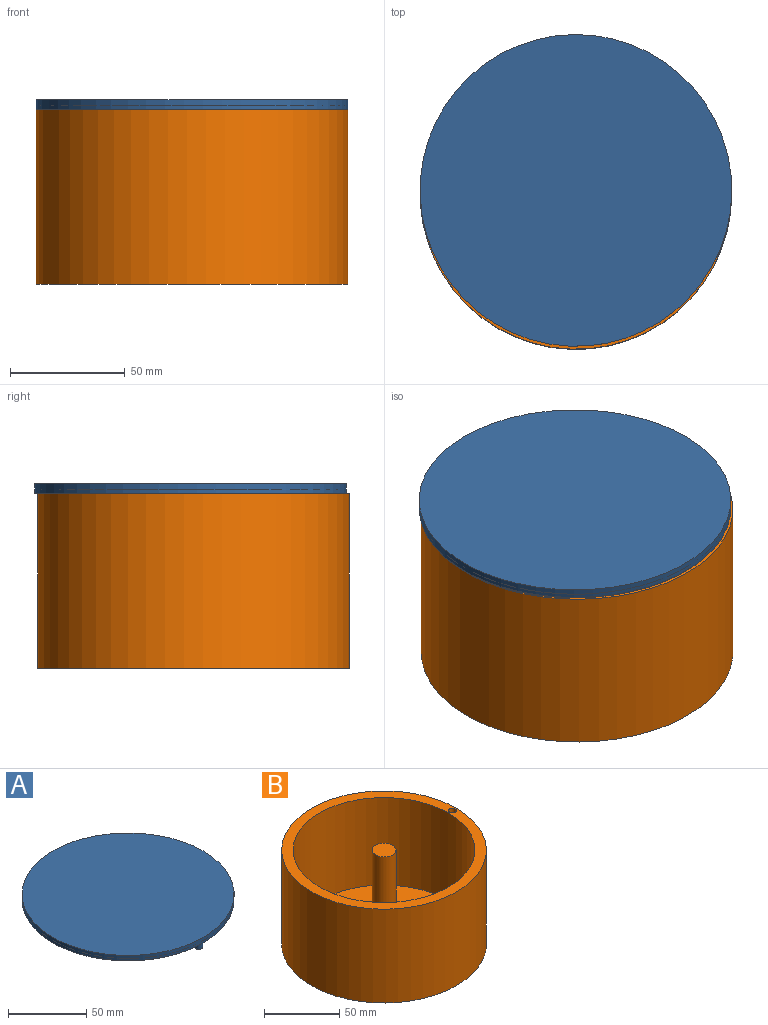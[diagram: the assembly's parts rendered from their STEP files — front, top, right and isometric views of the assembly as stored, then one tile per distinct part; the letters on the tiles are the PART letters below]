
ASSEMBLY  parts=2 mates=1
PART A: 9 faces, bbox 137.6x135.9x73.7 mm
  f0: torus R=4.95mm, axis (0,0,1), area 64.3mm2, adj f1,f5,f6,f7
  f1: cylinder r=2.41mm len=68.58mm, axis (0,0,-1), area 1039.8mm2, adj f0,f2,f6
  f2: plane 4.83x4.83mm, normal (0,0,-1), area 18.3mm2, adj f1
  f3: cylinder r=67.95mm len=135.89mm, axis (0,0,-1), area 1843.4mm2, adj f4,f8
  f4: plane 135.89x135.89mm, normal (0,0,1), area 14503.2mm2, adj f3
  f5: plane 135.26x135.16mm, normal (0,0,-1), area 14298.2mm2, adj f0,f7
  f6: bspline ~7.15x2.82mm, area 11.8mm2, adj f0,f1,f7
  f7: cylinder r=67.63mm len=135.26mm, axis (0,0,1), area 754.8mm2, adj f0,f5,f6,f8
  f8: plane 135.89x135.89mm, normal (0,0,-1), area 135.2mm2, adj f3,f7
PART B: 9 faces, bbox 135.9x135.9x76.2 mm
  f0: cylinder r=2.54mm len=71.12mm, axis (0,0,-1), area 1135mm2, adj f3,f8
  f1: cylinder r=60.32mm len=120.65mm, axis (0,0,-1), area 26956.8mm2, adj f3,f5
  f2: cylinder r=67.95mm len=135.89mm, axis (0,0,-1), area 32530.6mm2, adj f3,f4
  f3: plane 135.89x135.89mm, normal (0,0,1), area 3050.4mm2, adj f0,f1,f2
  f4: plane 135.89x135.89mm, normal (0,0,-1), area 14503.2mm2, adj f2
  f5: plane 120.65x120.65mm, normal (0,0,1), area 11234.7mm2, adj f1,f6
  f6: cylinder r=7.94mm len=71.12mm, axis (0,0,-1), area 3547mm2, adj f5,f7
  f7: plane 15.88x15.88mm, normal (0,0,1), area 197.9mm2, adj f6
  f8: plane 5.08x5.08mm, normal (0,0,1), area 20.3mm2, adj f0
PLACE A rot(axis=(0,0,-1),1.1deg) t=(279.47,-10.05,3.28)mm
PLACE B t=(113.63,-8.03,-3.65)mm fixed
MATE revolute A.f0 <-> B.f0  axis (0,0,-1) through (177.77,-8.03,72.55)mm
